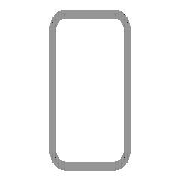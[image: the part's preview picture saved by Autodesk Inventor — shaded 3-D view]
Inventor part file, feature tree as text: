
AUTODESK INVENTOR PART (.ipt)
format: ipt  version: 2025.3 (Build 293356000, 356)  size: 133,632 bytes
history: native  units: mm (DEFAULTED — no unit token found)
features: other x4, sketch x1, plane x1
ambient origin geometry x8: Origin, YZ Plane, XZ Plane, XY Plane, X Axis, Y Axis, Z Axis, Center Point
bodies: Solid1 (feature_tree), Body (feature_tree)
feature tree (6):
  parser-record x1  (decoder bookkeeping rows leaked as tree rows — omitted from the tree; the rows remain in map.json)
  other  "Driven Length"
  other  "Start Plane"
  other  "End Plane"
  sketch  "Sketch3"  dims[d3=355.0mm d4=0.0mm d7=6.0mm d9=40.0mm d11=80.0mm d12=3.0mm d13=80.0mm d14=435.0mm d15=20.0mm d16=40.0mm d17=90.0deg d18=355.0mm]
  plane  "Work Plane3"
